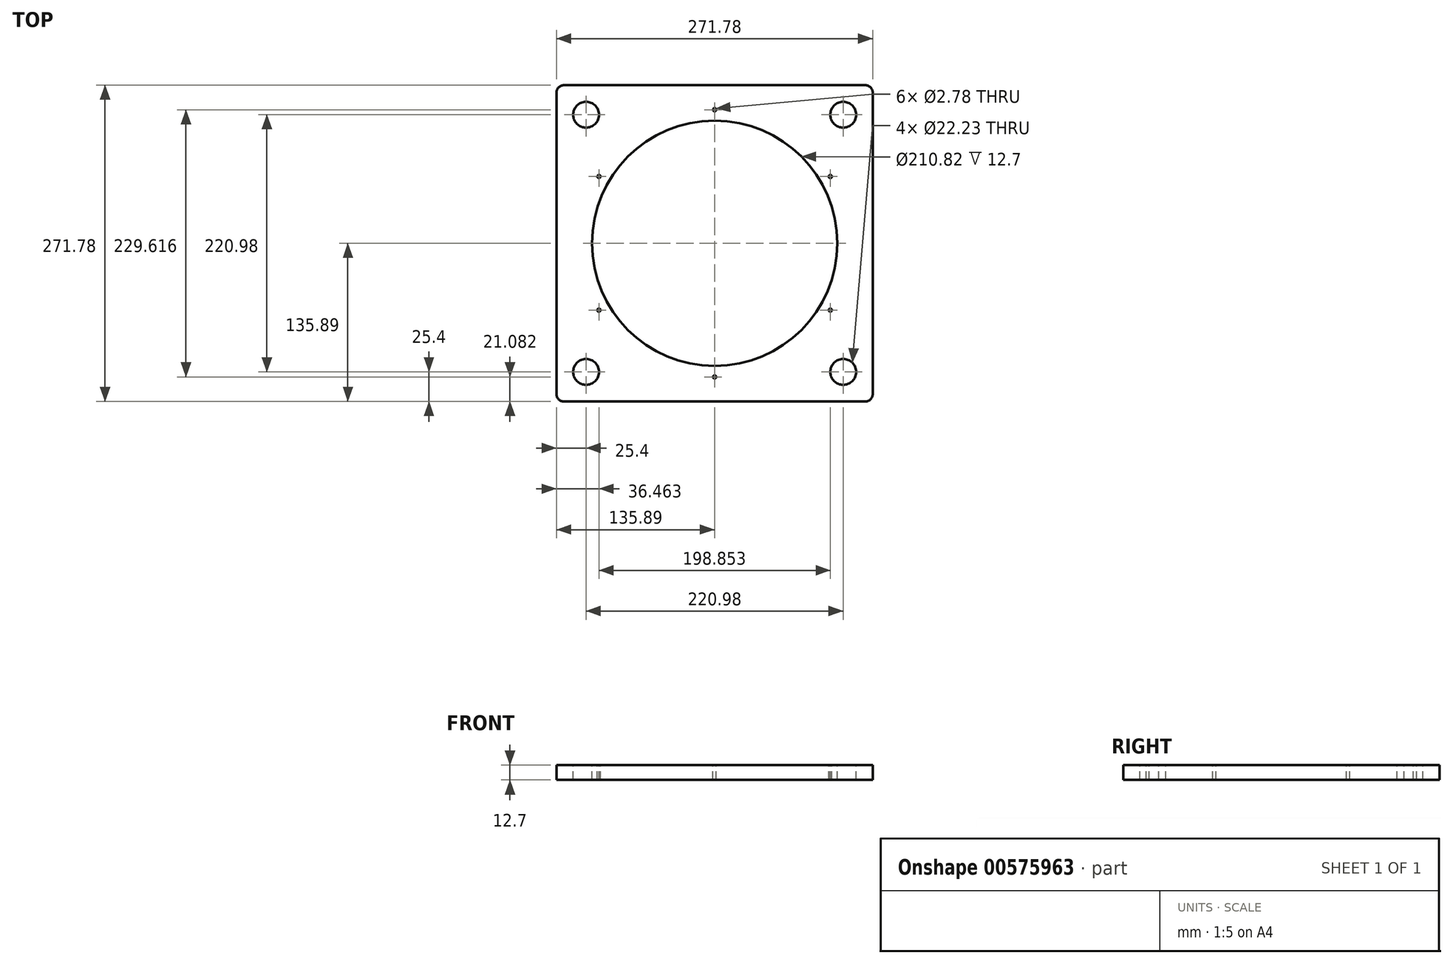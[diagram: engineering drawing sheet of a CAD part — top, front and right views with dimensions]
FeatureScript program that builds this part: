
annotation { "Feature Type Name" : "Feature", "Feature Type Description" : "" }
export const myFeature = defineFeature(function(context is Context, id is Id, definition is map)
    precondition{}
    {
        {
            var Q0;
            Q0=qCreatedBy(makeId("Top.planeOp"),FACE);
            var sketch = newSketch(context, id + "F0", { "sketchPlane" : qUnion([Q0])});
            skLineSegment(sketch, "E0.bottom", {"start": v(135.9, -135.89) * mm, "end": v(-135.9, -135.9) * mm});
            skLineSegment(sketch, "E0.top", {"start": v(135.9, 135.9) * mm, "end": v(-135.9, 135.89) * mm});
            skLineSegment(sketch, "E0.left", {"start": v(135.9, -135.89) * mm, "end": v(135.9, 135.9) * mm});
            skLineSegment(sketch, "E0.right", {"start": v(-135.9, -135.9) * mm, "end": v(-135.9, 135.89) * mm});
            skPoint(sketch, "E0.middle", {"position": v(0, 0) * mm});
            skSolve(sketch);
        }
        {
            var Q0;
            Q0 = qSketchRegion(id + "F0", true);
            extrude(context, id + "F1", {"entities" : qUnion([Q0]), "depth" : 12.7 * mm, "offsetDistance" : 25.4 * mm});
        }
        {
            var Q0;
            Q0=makeQuery(id+"F1.opExtrude","SWEPT_EDGE",EDGE,{"disambiguationData":[OSD([sQuery(id+"F0.wireOp",EDGE,"E0.bottom"),sQuery(id+"F0.wireOp",EDGE,"E0.right")])]});
            var Q1;
            Q1=makeQuery(id+"F1.opExtrude","SWEPT_EDGE",EDGE,{"disambiguationData":[OSD([sQuery(id+"F0.wireOp",EDGE,"E0.bottom"),sQuery(id+"F0.wireOp",EDGE,"E0.left")])]});
            var Q2;
            Q2=makeQuery(id+"F1.opExtrude","SWEPT_EDGE",EDGE,{"disambiguationData":[OSD([sQuery(id+"F0.wireOp",EDGE,"E0.top"),sQuery(id+"F0.wireOp",EDGE,"E0.right")])]});
            var Q3;
            Q3=makeQuery(id+"F1.opExtrude","SWEPT_EDGE",EDGE,{"disambiguationData":[OSD([sQuery(id+"F0.wireOp",EDGE,"E0.top"),sQuery(id+"F0.wireOp",EDGE,"E0.left")])]});
            fillet(context, id + "F2", {"entities" : qUnion([Q0, Q1, Q2, Q3]), "radius" : 6.35 * mm, "tangentPropagation" : true, "allowEdgeOverflow" : false});
        }
        {
            var Q0;
            Q0=makeQuery(id+"F1.opExtrude","CAP_FACE",FACE,{"disambiguationData":[OSD([sQuery(id+"F0.wireOp",EDGE,"E0.bottom"),sQuery(id+"F0.wireOp",EDGE,"E0.top"),sQuery(id+"F0.wireOp",EDGE,"E0.left"),sQuery(id+"F0.wireOp",EDGE,"E0.right")])],"isStart":false});
            var sketch = newSketch(context, id + "F3", { "sketchPlane" : qUnion([Q0])});
            skCircle(sketch, "E1", {"center": v(0, 0) * mm, "radius": 105.41 * mm});
            skSolve(sketch);
        }
        {
            var Q0;
            Q0 = qSketchRegion(id + "F3", true);
            extrude(context, id + "F4", {"entities" : qUnion([Q0]), "operationType" : NewBodyOperationType.REMOVE, "oppositeDirection" : true, "depth" : 25.4 * mm, "offsetDistance" : 25.4 * mm});
        }
        {
            var Q0;
            Q0=makeQuery(id+"F1.opExtrude","CAP_FACE",FACE,{"disambiguationData":[OSD([sQuery(id+"F0.wireOp",EDGE,"E0.bottom"),sQuery(id+"F0.wireOp",EDGE,"E0.top"),sQuery(id+"F0.wireOp",EDGE,"E0.left"),sQuery(id+"F0.wireOp",EDGE,"E0.right")])],"isStart":false});
            var sketch = newSketch(context, id + "F5", { "sketchPlane" : qUnion([Q0])});
            skCircle(sketch, "E2", {"center": v(0, 114.8) * mm, "radius": 1.39 * mm});
            skCircle(sketch, "E3.1.0", {"center": v(99.43, 57.4) * mm, "radius": 1.39 * mm});
            skCircle(sketch, "E3.2.0", {"center": v(99.43, -57.4) * mm, "radius": 1.39 * mm});
            skPoint(sketch, "E3.center", {"position": v(0, 0) * mm});
            skLineSegment(sketch, "E3.anchor1", {"start": v(0, 0) * mm, "end": v(0, 87.16) * mm, "construction": true});
            skLineSegment(sketch, "E3.anchor2", {"start": v(0, 0) * mm, "end": v(-99.43, 57.4) * mm, "construction": true});
            skCircle(sketch, "E4.1.3.0", {"center": v(0, -114.8) * mm, "radius": 1.39 * mm});
            skCircle(sketch, "E4.1.4.0", {"center": v(-99.43, -57.4) * mm, "radius": 1.39 * mm});
            skCircle(sketch, "E4.1.5.0", {"center": v(-99.43, 57.4) * mm, "radius": 1.39 * mm});
            skSolve(sketch);
        }
        {
            var Q0;
            Q0 = qSketchRegion(id + "F5", true);
            extrude(context, id + "F6", {"entities" : qUnion([Q0]), "operationType" : NewBodyOperationType.REMOVE, "oppositeDirection" : true, "depth" : 25.4 * mm, "offsetDistance" : 25.4 * mm});
        }
        {
            var Q0;
            Q0=makeQuery(id+"F1.opExtrude","CAP_FACE",FACE,{"disambiguationData":[OSD([sQuery(id+"F0.wireOp",EDGE,"E0.bottom"),sQuery(id+"F0.wireOp",EDGE,"E0.top"),sQuery(id+"F0.wireOp",EDGE,"E0.left"),sQuery(id+"F0.wireOp",EDGE,"E0.right")])],"isStart":false});
            var sketch = newSketch(context, id + "F7", { "sketchPlane" : qUnion([Q0])});
            skCircle(sketch, "E5", {"center": v(-110.49, 110.5) * mm, "radius": 11.11 * mm});
            skCircle(sketch, "E6.MirrorC", {"center": v(110.49, 110.5) * mm, "radius": 11.11 * mm});
            skCircle(sketch, "E7.MirrorC", {"center": v(110.49, -110.5) * mm, "radius": 11.11 * mm});
            skCircle(sketch, "E8.MirrorC", {"center": v(-110.49, -110.5) * mm, "radius": 11.11 * mm});
            skSolve(sketch);
        }
        {
            var Q0;
            Q0 = qSketchRegion(id + "F7", true);
            extrude(context, id + "F8", {"entities" : qUnion([Q0]), "operationType" : NewBodyOperationType.REMOVE, "oppositeDirection" : true, "depth" : 25.4 * mm, "offsetDistance" : 25.4 * mm});
        }
    });
